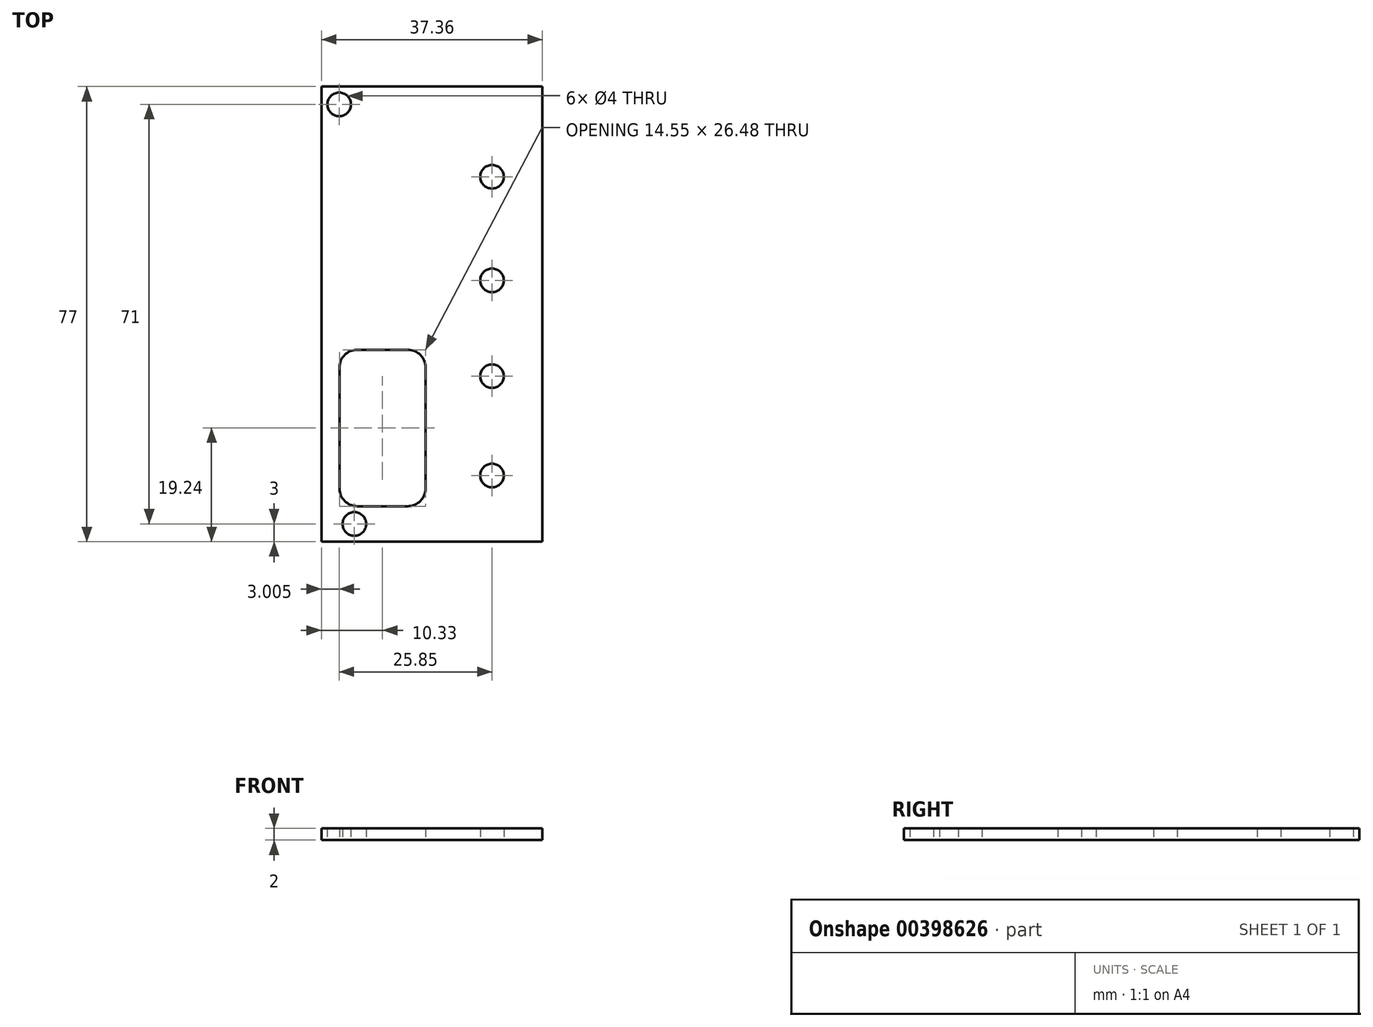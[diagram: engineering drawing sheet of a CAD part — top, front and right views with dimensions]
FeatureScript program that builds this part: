
annotation { "Feature Type Name" : "Feature", "Feature Type Description" : "" }
export const myFeature = defineFeature(function(context is Context, id is Id, definition is map)
    precondition{}
    {
        {
            var Q0;
            Q0=qCreatedBy(makeId("Top.planeOp"),FACE);
            var sketch = newSketch(context, id + "F0", { "sketchPlane" : qUnion([Q0])});
            skLineSegment(sketch, "E0.bottom", {"start": v(-18.67, 38.5) * mm, "end": v(18.68, 38.5) * mm});
            skLineSegment(sketch, "E0.top", {"start": v(-18.68, -38.5) * mm, "end": v(18.68, -38.5) * mm});
            skLineSegment(sketch, "E0.left", {"start": v(-18.67, 38.5) * mm, "end": v(-18.68, -38.5) * mm});
            skLineSegment(sketch, "E0.right", {"start": v(18.68, 38.5) * mm, "end": v(18.68, -38.5) * mm});
            skPoint(sketch, "E0.middle", {"position": v(0, 0) * mm});
            skLineSegment(sketch, "E1.bottom", {"start": v(-15.63, -32.5) * mm, "end": v(-1.07, -32.5) * mm});
            skLineSegment(sketch, "E1.top", {"start": v(-15.63, -6.02) * mm, "end": v(-1.07, -6.02) * mm});
            skLineSegment(sketch, "E1.left", {"start": v(-15.62, -32.5) * mm, "end": v(-15.62, -6.02) * mm});
            skLineSegment(sketch, "E1.right", {"start": v(-1.07, -32.5) * mm, "end": v(-1.07, -6.02) * mm});
            skCircle(sketch, "E2", {"center": v(-13.1, -35.5) * mm, "radius": 2 * mm});
            skCircle(sketch, "E3", {"center": v(10.18, 23.25) * mm, "radius": 2 * mm});
            skCircle(sketch, "E4", {"center": v(10.18, 5.72) * mm, "radius": 2 * mm});
            skCircle(sketch, "E5", {"center": v(10.18, -10.5) * mm, "radius": 2 * mm});
            skCircle(sketch, "E6", {"center": v(10.18, -27.3) * mm, "radius": 2 * mm});
            skCircle(sketch, "E7", {"center": v(-15.67, 35.5) * mm, "radius": 2 * mm});
            skSolve(sketch);
        }
        {
            var Q0;
            Q0=makeQuery(id+"F0.imprint","IMPRINT",FACE,{"disambiguationData":[TD([[makeQuery(id+"F0.imprint","IMPRINT",EDGE,{"derivedFrom":sQuery(id+"F0.wireOp",EDGE,"E0.bottom")}),-1.0]])]});
            extrude(context, id + "F1", {"entities" : qUnion([Q0]), "depth" : 2 * mm});
        }
        {
            var Q0;
            Q0=makeQuery(id+"F1.opExtrude","SWEPT_EDGE",EDGE,{"disambiguationData":[OSD([sQuery(id+"F0.wireOp",EDGE,"E1.top"),sQuery(id+"F0.wireOp",EDGE,"E1.right")])]});
            var Q1;
            Q1=makeQuery(id+"F1.opExtrude","SWEPT_EDGE",EDGE,{"disambiguationData":[OSD([sQuery(id+"F0.wireOp",EDGE,"E1.bottom"),sQuery(id+"F0.wireOp",EDGE,"E1.right")])]});
            var Q2;
            Q2=makeQuery(id+"F1.opExtrude","SWEPT_EDGE",EDGE,{"disambiguationData":[OSD([sQuery(id+"F0.wireOp",EDGE,"E1.bottom"),sQuery(id+"F0.wireOp",EDGE,"E1.left")])]});
            var Q3;
            Q3=makeQuery(id+"F1.opExtrude","SWEPT_EDGE",EDGE,{"disambiguationData":[OSD([sQuery(id+"F0.wireOp",EDGE,"E1.top"),sQuery(id+"F0.wireOp",EDGE,"E1.left")])]});
            fillet(context, id + "F2", {"entities" : qUnion([Q0, Q1, Q2, Q3]), "radius" : 3 * mm, "tangentPropagation" : true, "allowEdgeOverflow" : false});
        }
        {
            var Q0;
            Q0=makeQuery(id+"F1.opExtrude","SWEPT_EDGE",EDGE,{"disambiguationData":[OSD([sQuery(id+"F0.wireOp",EDGE,"E0.top"),sQuery(id+"F0.wireOp",EDGE,"E0.left")])]});
            var Q1;
            Q1=makeQuery(id+"F1.opExtrude","SWEPT_EDGE",EDGE,{"disambiguationData":[OSD([sQuery(id+"F0.wireOp",EDGE,"E0.top"),sQuery(id+"F0.wireOp",EDGE,"E0.right")])]});
            var Q2;
            Q2=makeQuery(id+"F1.opExtrude","SWEPT_EDGE",EDGE,{"disambiguationData":[OSD([sQuery(id+"F0.wireOp",EDGE,"E0.bottom"),sQuery(id+"F0.wireOp",EDGE,"E0.right")])]});
            var Q3;
            Q3=makeQuery(id+"F1.opExtrude","SWEPT_EDGE",EDGE,{"disambiguationData":[OSD([sQuery(id+"F0.wireOp",EDGE,"E0.bottom"),sQuery(id+"F0.wireOp",EDGE,"E0.left")])]});
            fillet(context, id + "F3", {"entities" : qUnion([Q0, Q1, Q2, Q3]), "radius" : 1 * mm, "tangentPropagation" : true, "allowEdgeOverflow" : false});
        }
        {
            var Q0;
            Q0 = qSketchRegion(id + "F0", true);
            var Q1;
            Q1=makeQuery(id+"FXXe4dsuCKhccT3_1.imprint","IMPRINT",FACE,{"disambiguationData":[TD([[makeQuery(id+"FXXe4dsuCKhccT3_1.imprint","IMPRINT",EDGE,{"derivedFrom":sQuery(id+"FXXe4dsuCKhccT3_1.wireOp",EDGE,"43T6hMFa-2wOP-IDeT-wEf4-1eukB9OrjBIe.bottom")}),-1.0]])]});
            extrude(context, id + "F4", {"entities" : qUnion([Q0, Q1]), "operationType" : NewBodyOperationType.ADD, "depth" : 2 * mm});
        }
    });
